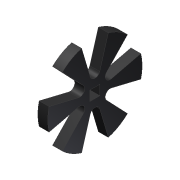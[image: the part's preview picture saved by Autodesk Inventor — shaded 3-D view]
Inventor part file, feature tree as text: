
AUTODESK INVENTOR PART (.ipt)
format: ipt  version: 2012 (Build 160160000, 160)  size: 123,904 bytes
history: native  units: in
note: dims shown in document units (in); Inventor stores cm internally (conversion verified against a paired STEP export)
features: extrude x2, sketch x2, pattern_circular x1
ambient origin geometry x8: Origin, YZ Plane, XZ Plane, XY Plane, X Axis, Y Axis, Z Axis, Center Point
bodies: Solid1 (feature_tree)
feature tree (5):
  extrude  "Extrusion1"  Depth=0.5in
  extrude  "Extrusion3"  Depth=0.2257in
  pattern_circular  "Circular Pattern2"  [2 undecoded]
  sketch  "Sketch1"  dims[d0=4.75in d1=0.5in]
  sketch  "Sketch2"  dims[d2=0.5in d3=0.0in d4=0.2257in d11=0.0625in d12=1.75in d13=1.0in d14=0.0in d15=3.937in d16=360.0deg]
note: 2 required parameter values undecoded (feature->parameter linkage not recoverable at this tier; creation-order binding heuristic only, values carry confidence <= 0.55)
